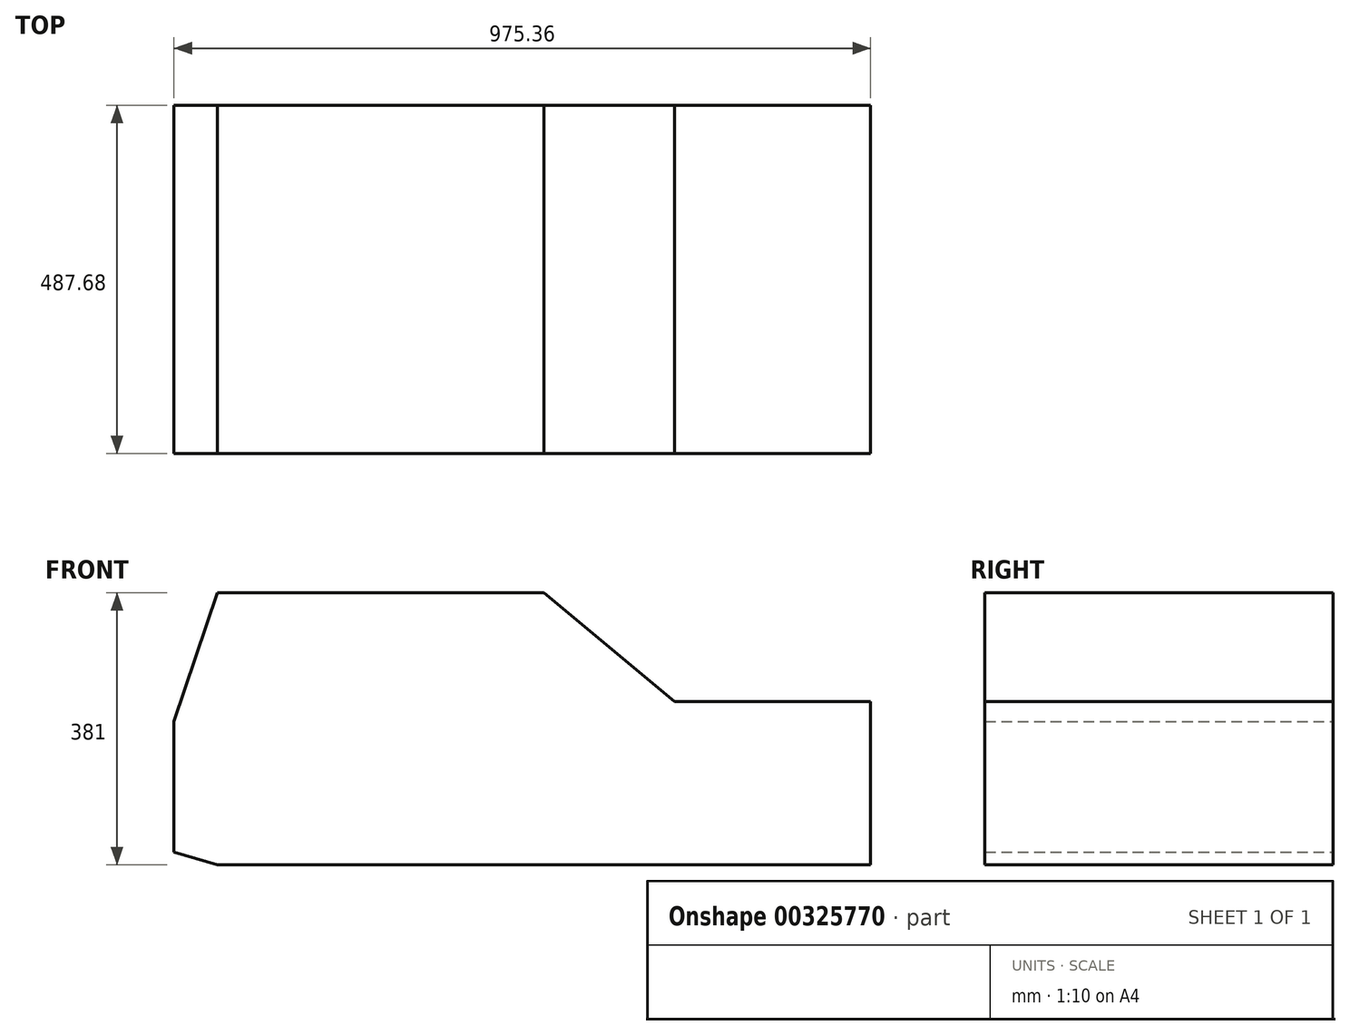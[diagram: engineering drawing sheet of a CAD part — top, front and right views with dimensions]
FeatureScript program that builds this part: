
annotation { "Feature Type Name" : "Feature", "Feature Type Description" : "" }
export const myFeature = defineFeature(function(context is Context, id is Id, definition is map)
    precondition{}
    {
        {
            var Q0;
            Q0=qCreatedBy(makeId("Front.planeOp"),FACE);
            var sketch = newSketch(context, id + "F0", { "sketchPlane" : qUnion([Q0])});
            skLineSegment(sketch, "E0.bottom", {"start": v(62.43, 180.02) * mm, "end": v(-394.77, 180.02) * mm});
            skLineSegment(sketch, "E0.top", {"start": v(62.43, -200.98) * mm, "end": v(-394.77, -200.98) * mm});
            skLineSegment(sketch, "E0.left", {"start": v(62.43, 180.02) * mm, "end": v(62.43, -200.98) * mm});
            skLineSegment(sketch, "E0.right", {"start": v(-394.77, 180.02) * mm, "end": v(-394.77, -200.98) * mm});
            skLineSegment(sketch, "E1", {"start": v(-394.77, 180.02) * mm, "end": v(-455.73, 0) * mm});
            skLineSegment(sketch, "E2", {"start": v(-455.73, 0) * mm, "end": v(-455.73, 0) * mm});
            skLineSegment(sketch, "E3", {"start": v(-455.73, 0) * mm, "end": v(-455.73, -182.88) * mm});
            skLineSegment(sketch, "E4", {"start": v(-455.73, -182.88) * mm, "end": v(-394.77, -200.98) * mm});
            skLineSegment(sketch, "E5", {"start": v(62.43, 180.02) * mm, "end": v(245.3, 27.62) * mm});
            skLineSegment(sketch, "E6", {"start": v(245.3, 27.62) * mm, "end": v(519.63, 27.62) * mm});
            skLineSegment(sketch, "E7", {"start": v(519.63, 27.62) * mm, "end": v(519.63, -200.98) * mm});
            skLineSegment(sketch, "E8", {"start": v(519.63, -200.98) * mm, "end": v(62.43, -200.98) * mm});
            skSolve(sketch);
        }
        {
            var Q0;
            Q0 = qSketchRegion(id + "F0", true);
            extrude(context, id + "F1", {"entities" : qUnion([Q0]), "depth" : 487.68 * mm});
        }
    });
